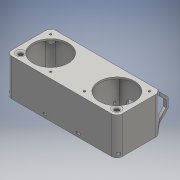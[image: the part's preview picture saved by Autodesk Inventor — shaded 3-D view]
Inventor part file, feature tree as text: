
AUTODESK INVENTOR PART (.ipt)
format: ipt  version: 2016 (Build 200138000, 138)  size: 761,344 bytes
history: native  units: mm
features: sketch x23, extrude x20, projected_geometry x20, reference x10, mirror x4, hole x3, plane x3, fillet x2, chamfer x1
ambient origin geometry x8: Origin, YZ Plane, XZ Plane, XY Plane, X Axis, Y Axis, Z Axis, Center Point
bodies: Solid1 (feature_tree)
feature tree (86):
  extrude  "Extrusion1"  Depth=100.0mm
  extrude  "Extrusion2"  Depth=80.0mm
  extrude  "Extrusion3"  Depth=50.0mm
  hole  "Hole1"  [1 undecoded]
  extrude  "Extrusion4"  Depth=100.0mm
  extrude  "Extrusion5"  Depth=92.0mm
  mirror  "Mirror1"
  fillet  "Fillet1"  Radius=80.0mm
  extrude  "Extrusion6"  TaperAngle=45.0deg  [1 undecoded]
  extrude  "Extrusion7"  Depth=15.0mm
  extrude  "Extrusion8"  Depth=10.0mm TaperAngle=0.0deg
  mirror  "Mirror2"
  plane  "Work Plane1"
  extrude  "Extrusion9"  Depth=7.0mm
  extrude  "Extrusion10"  Depth=5.0mm
  hole  "Hole2"  [1 undecoded]
  mirror  "Mirror3"
  extrude  "Extrusion11"  Depth=5.0mm TaperAngle=0.0deg
  extrude  "Extrusion12"  Depth=15.0mm
  extrude  "Extrusion13"  Depth=3.0mm
  hole  "Hole3"  [1 undecoded]
  plane  "Work Plane2"
  extrude  "Extrusion14"  Depth=10.0mm TaperAngle=0.0deg
  extrude  "Extrusion15"  Depth=10.0mm
  extrude  "Extrusion16"  Depth=10.0mm
  extrude  "Extrusion17"  Depth=10.0mm
  extrude  "Extrusion18"  Depth=7.5mm
  extrude  "Extrusion19"  Depth=7.5mm
  plane  "Work Plane3"
  extrude  "Extrusion20"  Depth=5.0mm
  mirror  "Mirror4"
  chamfer  "Chamfer2"  Distance=10.5mm
  fillet  "Fillet3"  Radius=7.5mm
  sketch  "Sketch1"  dims[d0=250.0mm d1=100.0mm]
  sketch  "Sketch2"  dims[d2=4.0mm d3=0.0mm d4=80.0mm]
  sketch  "Sketch3"  dims[d5=80.0mm d6=50.0mm]
  projected_geometry  "Projected Loop1"
  sketch  "Sketch4"  dims[d7=50.0mm d8=4.0mm d9=0.0mm]
  projected_geometry  "Projected Loop2"
  sketch  "Sketch5"  dims[d10=250.0mm d11=100.0mm]
  projected_geometry  "Projected Loop3"
  sketch  "Sketch6"  dims[d12=242.0mm d13=92.0mm d14=80.0mm d15=0.0mm]
  projected_geometry  "Projected Loop4"
  projected_geometry  "Projected Loop5"
  sketch  "Sketch7"  dims[d16=104.0mm d17=45.0deg]
  projected_geometry  "Projected Loop6"
  sketch  "Sketch8"  dims[d18=4.5mm d19=6.0mm d20=4.0mm d21=2.0mm d22=90.0deg d23=8.0mm d24=20.594885mm d25=15.0mm]
  projected_geometry  "Projected Loop7"
  sketch  "Sketch9"  dims[d26=15.0mm d27=10.0mm d28=0.0mm]
  projected_geometry  "Projected Loop8"
  sketch  "Sketch10"  dims[d29=7.0mm d30=7.0mm]
  projected_geometry  "Projected Loop9"
  projected_geometry  "Projected Loop10"
  projected_geometry  "Projected Loop11"
  sketch  "Sketch11"  dims[d31=5.0mm d32=0.0mm d33=12.0mm]
  projected_geometry  "Projected Loop12"
  sketch  "Sketch12"  dims[d34=6.0mm d35=1.0mm]
  sketch  "Sketch13"  dims[d36=4.0mm d37=5.0mm d38=0.0mm]
  sketch  "Sketch14"  dims[d39=15.0mm d40=15.0mm]
  projected_geometry  "Projected Loop13"
  sketch  "Sketch15"  dims[d41=45.0deg d42=3.0mm]
  reference  "Reference1"
  reference  "Reference2"
  reference  "Reference3"
  reference  "Reference4"
  projected_geometry  "Projected Loop14"
  sketch  "Sketch16"  dims[d43=15.0mm d44=38.0mm d45=0.0mm]
  projected_geometry  "Projected Loop15"
  projected_geometry  "Projected Loop16"
  projected_geometry  "Projected Loop17"
  projected_geometry  "Projected Loop18"
  sketch  "Sketch17"  dims[d46=10.0mm d47=38.0mm d48=0.0mm]
  projected_geometry  "Projected Loop19"
  projected_geometry  "Projected Loop20"
  sketch  "Sketch18"  dims[d49=-10.0mm d50=10.0mm]
  reference  "Reference5"
  reference  "Reference6"
  reference  "Reference7"
  reference  "Reference8"
  reference  "Reference9"
  reference  "Reference10"
  sketch  "Sketch19"  dims[d51=15.0mm d52=10.0mm]
  sketch  "Sketch20"  dims[d53=10.0mm d54=0.0mm d55=7.0mm]
  sketch  "Sketch21"  dims[d56=7.5mm d57=7.5mm]
  sketch  "Sketch22"  dims[d58=7.0mm d59=7.5mm]
  sketch  "Sketch23"  dims[d60=7.5mm d61=7.0mm d63=10.5mm d64=7.5mm d65=7.0mm d66=4.0mm d67=0.0mm d68=4.5mm d69=6.0mm d70=4.0mm d71=2.0mm d72=90.0deg d73=8.0mm d74=20.594885mm d75=142.0mm d76=43.0mm d77=20.5mm d78=0.0mm d79=10.0mm d80=21.0mm d81=0.0mm d82=10.0mm d83=0.0mm d84=3.5mm d85=6.0mm d86=4.0mm d87=2.0mm d88=90.0deg d89=10.0mm d90=0.0mm d91=-6.0mm d92=5.7mm d93=5.7mm d94=5.7mm d95=5.7mm d96=2.5mm d97=0.0mm d98=9.5mm d99=6.0mm d100=5.75mm d101=0.0mm d102=8.0mm d103=29.0mm d104=5.75mm d105=0.0mm d106=6.0mm d107=76.25mm d108=0.0mm d109=20.25mm d110=23.5mm d111=0.0mm d113=20.25mm d114=7.0mm d115=23.5mm d116=0.0mm d117=40.0mm d118=135.0deg d119=3.0mm d120=40.0mm d121=135.0deg d122=3.0mm d123=8.0mm d124=5.0mm d125=8.0mm d126=5.0mm d127=6.0mm d128=0.0mm d132=8.0mm d133=2.0mm d134=45.0deg d135=5.0mm]
note: 4 required parameter values undecoded (feature->parameter linkage not recoverable at this tier; creation-order binding heuristic only, values carry confidence <= 0.55)
